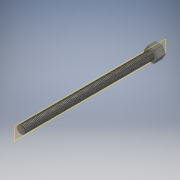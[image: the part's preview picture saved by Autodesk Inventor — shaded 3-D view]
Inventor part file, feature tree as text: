
AUTODESK INVENTOR PART (.ipt)
format: ipt  version: 2019 (Build 230136000, 136)  size: 857,600 bytes
history: native  units: mm
features: sketch x3, extrude x2, helix x1
ambient origin geometry x8: Origin, YZ Plane, XZ Plane, XY Plane, X Axis, Y Axis, Z Axis, Center Point
bodies: Solid1 (feature_tree)
feature tree (6):
  extrude  "Extrusion1"  Depth=118.75mm TaperAngle=0.0deg
  extrude  "Extrusion2"  Depth=5.369358mm
  helix  "Coil1"  [1 undecoded]
  sketch  "Sketch1"  dims[d0=7.0mm d1=118.75mm d2=0.0mm]
  sketch  "Sketch2"  dims[d3=12.4mm d4=5.369358mm d5=7.5mm d6=0.0mm]
  sketch  "Sketch3"  dims[d7=0.5mm d8=0.5mm d9=10.0mm d10=118.75mm d11=1000.0mm d12=0.0mm d13=90.0deg d14=90.0deg d15=0.0mm d16=0.0mm]
note: 1 required parameter value undecoded (feature->parameter linkage not recoverable at this tier; creation-order binding heuristic only, values carry confidence <= 0.55)
